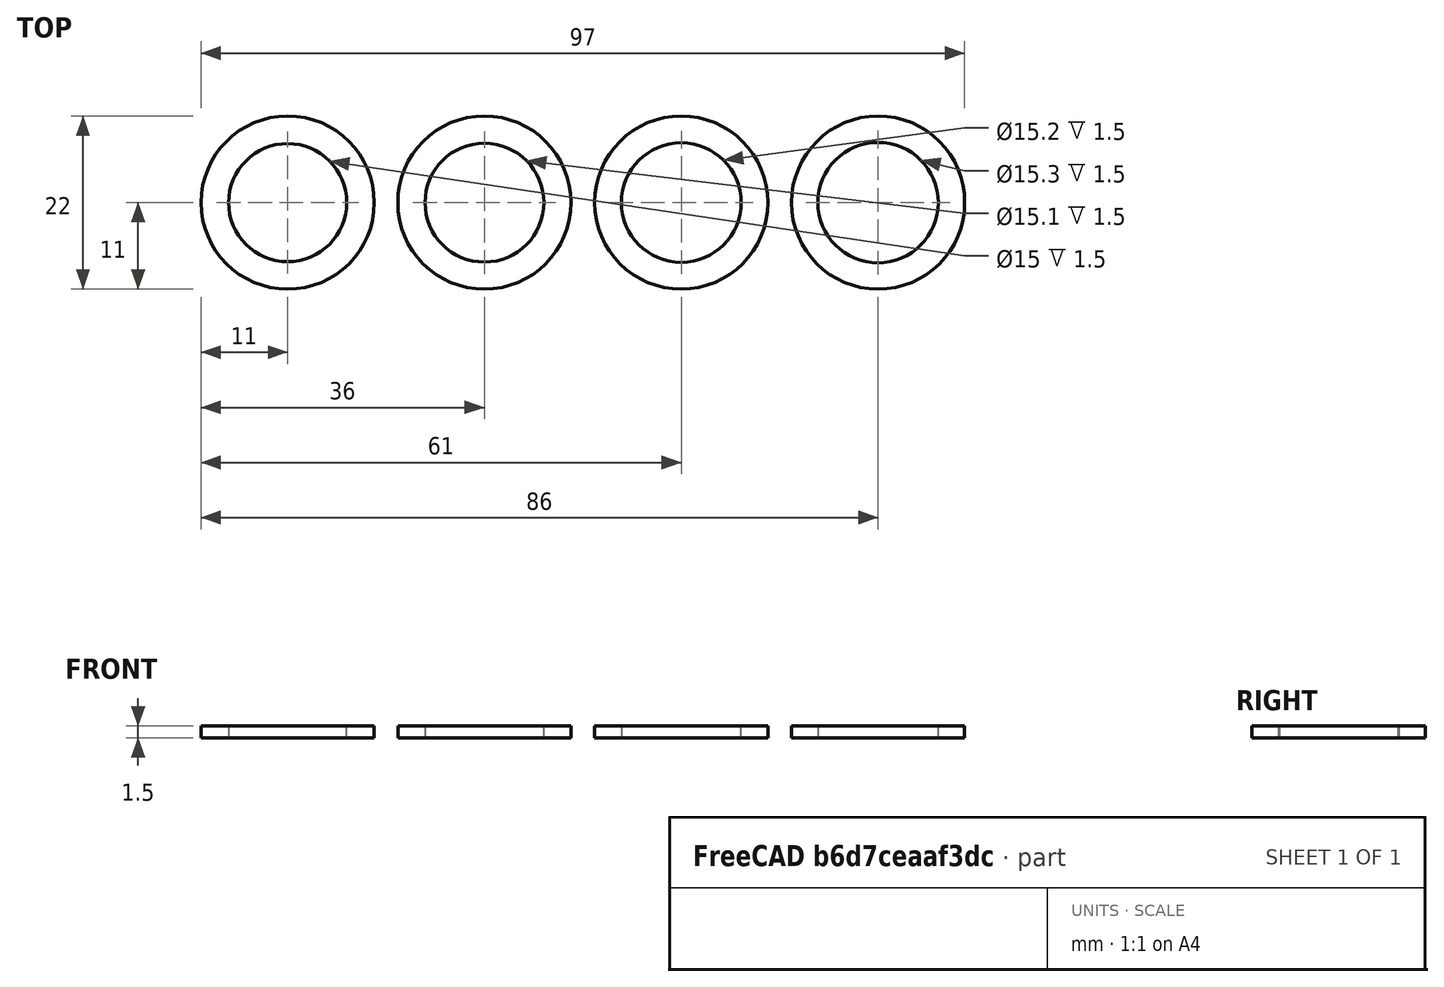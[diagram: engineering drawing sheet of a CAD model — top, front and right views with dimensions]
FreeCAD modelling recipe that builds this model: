
FCSTD DOCUMENT  (FreeCAD 0.16R)
Label: washers
License: All rights reserved
LicenseURL: http://en.wikipedia.org/wiki/All_rights_reserved
objects: Sketcher::SketchObject×2, PartDesign::Pad×1, Mesh::Feature×1
note: 4 computed .brp shape members not serialized (recipe doc carries the construction recipe); baked Part::Feature solids carry a one-line shape summary decoded from their .brp

FEATURE [Sketcher::SketchObject] Sketch
  sketch-geometry (8):
    g0: Circle CenterX=-50 CenterY=0 CenterZ=0 NormalX=0 NormalY=0 NormalZ=1 Radius=11
    g1: Circle CenterX=-25 CenterY=0 CenterZ=0 NormalX=0 NormalY=0 NormalZ=1 Radius=11
    g2: Circle CenterX=0 CenterY=0 CenterZ=0 NormalX=0 NormalY=0 NormalZ=1 Radius=11
    g3: Circle CenterX=25 CenterY=0 CenterZ=0 NormalX=0 NormalY=0 NormalZ=1 Radius=11
    g4: Circle CenterX=-50 CenterY=0 CenterZ=0 NormalX=0 NormalY=0 NormalZ=1 Radius=7.5
    g5: Circle CenterX=-25 CenterY=0 CenterZ=0 NormalX=0 NormalY=0 NormalZ=1 Radius=7.55
    g6: Circle CenterX=0 CenterY=0 CenterZ=0 NormalX=0 NormalY=0 NormalZ=1 Radius=7.6
    g7: Circle CenterX=25 CenterY=0 CenterZ=0 NormalX=0 NormalY=0 NormalZ=1 Radius=7.65
  constraints (20):
    c: Radius(g0) = 11
    c: Equal(g0,g1)
    c: Equal(g0,g2)
    c: Equal(g0,g3)
    c: PointOnObject(g6,g-2)
    c: Radius(g4) = 7.5
    c: Radius(g5) = 7.55
    c: Radius(g6) = 7.6
    c: Radius(g7) = 7.65
    c: Coincident(g4,g0)
    c: Coincident(g5,g1)
    c: Coincident(g2,g6)
    c: Coincident(g3,g7)
    c: PointOnObject(g0,g-1)
    c: PointOnObject(g1,g-1)
    c: PointOnObject(g2,g-1)
    c: PointOnObject(g3,g-1)
    c: DistanceX(g0,g1) = 25
    c: DistanceX(g1,g-1) = 25
    c: DistanceX(g-1,g3) = 25
FEATURE [PartDesign::Pad] Pad
  Length = 1.5
  Length2 = 100
  Sketch = -> Sketch
  Type = 0
FEATURE [Sketcher::SketchObject] Sketch001
  sketch-geometry (8):
    g0: Circle CenterX=-50 CenterY=0 CenterZ=0 NormalX=0 NormalY=0 NormalZ=1 Radius=11
    g1: Circle CenterX=-25 CenterY=0 CenterZ=0 NormalX=0 NormalY=0 NormalZ=1 Radius=11
    g2: Circle CenterX=0 CenterY=0 CenterZ=0 NormalX=0 NormalY=0 NormalZ=1 Radius=11
    g3: Circle CenterX=25 CenterY=0 CenterZ=0 NormalX=0 NormalY=0 NormalZ=1 Radius=11
    g4: Circle CenterX=-50 CenterY=0 CenterZ=0 NormalX=0 NormalY=0 NormalZ=1 Radius=7.5
    g5: Circle CenterX=-25 CenterY=0 CenterZ=0 NormalX=0 NormalY=0 NormalZ=1 Radius=7.55
    g6: Circle CenterX=0 CenterY=0 CenterZ=0 NormalX=0 NormalY=0 NormalZ=1 Radius=7.6
    g7: Circle CenterX=25 CenterY=0 CenterZ=0 NormalX=0 NormalY=0 NormalZ=1 Radius=7.65
  constraints (11):
    c: Radius(g0) = 11
    c: Equal(g0,g1)
    c: Equal(g0,g2)
    c: Equal(g0,g3)
    c: Radius(g4) = 7.5
    c: Radius(g5) = 7.55
    c: Radius(g6) = 7.6
    c: Radius(g7) = 7.65
    c: DistanceX(g0,g1) = 25
    c: DistanceX(g1,g-1) = 25
    c: DistanceX(g-1,g3) = 25
FEATURE [Mesh::Feature] Mesh  label="Pad (Meshed)"
